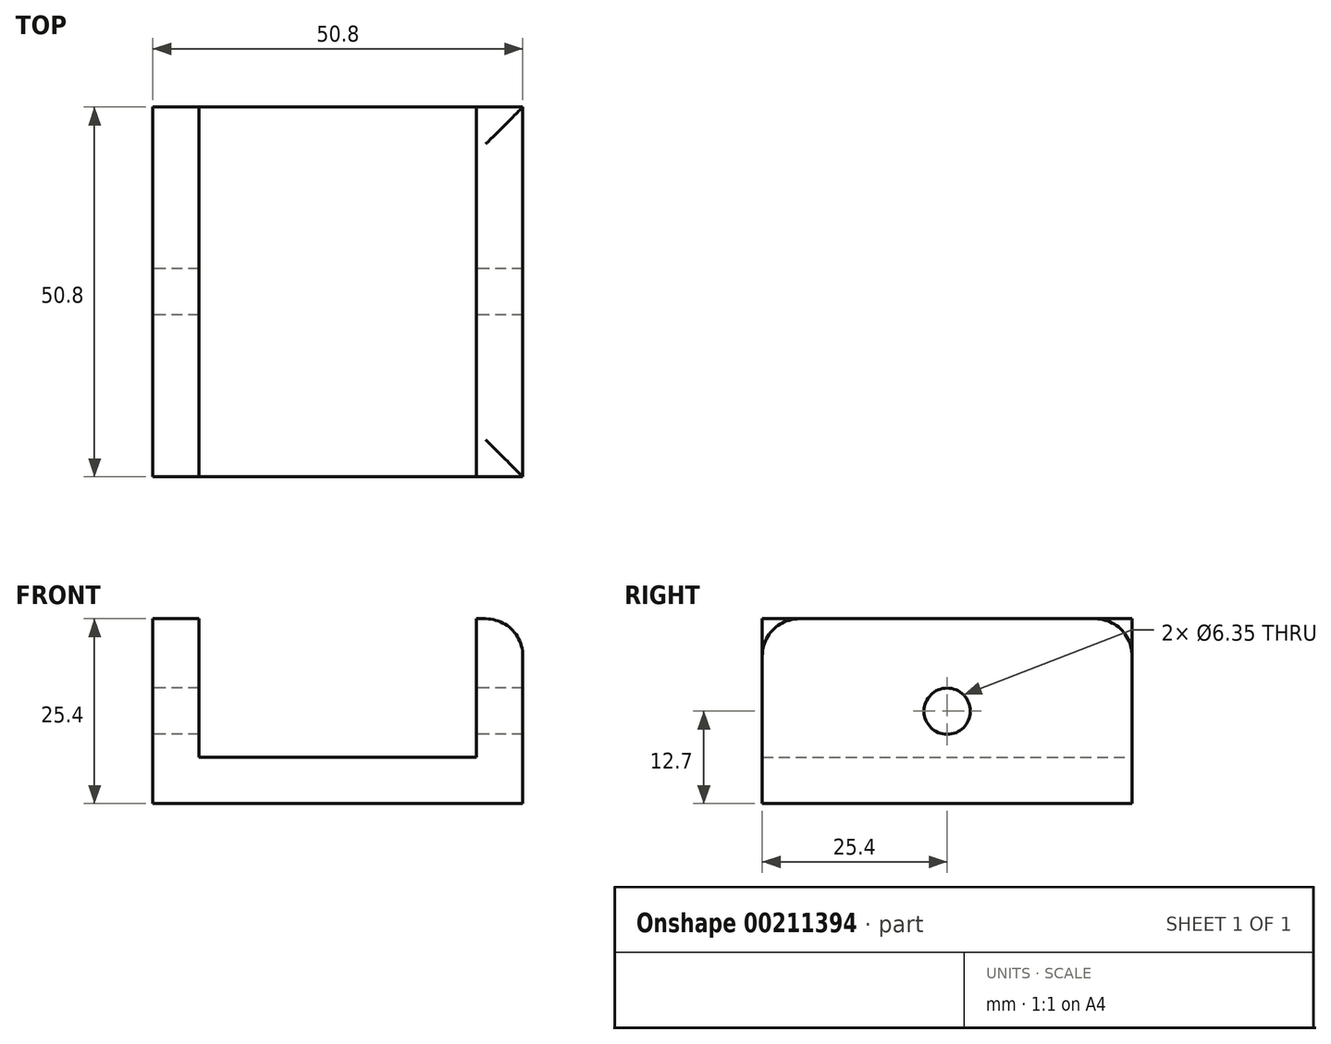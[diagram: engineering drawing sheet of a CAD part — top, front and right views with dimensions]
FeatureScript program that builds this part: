
annotation { "Feature Type Name" : "Feature", "Feature Type Description" : "" }
export const myFeature = defineFeature(function(context is Context, id is Id, definition is map)
    precondition{}
    {
        {
            var Q0;
            Q0=qCreatedBy(makeId("Front.planeOp"),FACE);
            var sketch = newSketch(context, id + "F0", { "sketchPlane" : qUnion([Q0])});
            skLineSegment(sketch, "E0", {"start": v(6.35, 25.4) * mm, "end": v(0, 25.4) * mm});
            skLineSegment(sketch, "E1", {"start": v(0, 25.4) * mm, "end": v(0, 0) * mm});
            skLineSegment(sketch, "E2", {"start": v(0, 0) * mm, "end": v(50.8, 0) * mm});
            skLineSegment(sketch, "E3", {"start": v(50.8, 0) * mm, "end": v(50.8, 25.4) * mm});
            skLineSegment(sketch, "E4", {"start": v(50.8, 25.4) * mm, "end": v(44.45, 25.4) * mm});
            skLineSegment(sketch, "E5", {"start": v(44.45, 25.4) * mm, "end": v(44.45, 6.35) * mm});
            skLineSegment(sketch, "E6", {"start": v(44.45, 6.35) * mm, "end": v(6.35, 6.35) * mm});
            skLineSegment(sketch, "E7", {"start": v(6.35, 6.35) * mm, "end": v(6.35, 25.4) * mm});
            skSolve(sketch);
        }
        {
            var Q0;
            Q0 = qSketchRegion(id + "F0", true);
            extrude(context, id + "F1", {"entities" : qUnion([Q0]), "depth" : 50.8 * mm});
        }
        {
            var Q0;
            Q0=makeQuery(id+"F1.opExtrude","SWEPT_FACE",FACE,{"disambiguationData":[OSD([sQuery(id+"F0.wireOp",EDGE,"E1")])]});
            var sketch = newSketch(context, id + "F2", { "sketchPlane" : qUnion([Q0])});
            skCircle(sketch, "E8", {"center": v(25.4, 12.7) * mm, "radius": 3.18 * mm});
            skPoint(sketch, "E8.centerSnap0", {"position": v(50.8, 12.7) * mm});
            skPoint(sketch, "E8.centerSnap1", {"position": v(25.4, 25.4) * mm});
            skSolve(sketch);
        }
        {
            var Q0;
            Q0=sQuery(id+"F2.wireOp",VERTEX,"E8.center");
            var Q1;
            Q1=makeQuery(id+"F1.opExtrude","SWEPT_BODY",BODY,{"disambiguationData":[OSD([sQuery(id+"F0.wireOp",EDGE,"E0"),sQuery(id+"F0.wireOp",EDGE,"E1"),sQuery(id+"F0.wireOp",EDGE,"E2"),sQuery(id+"F0.wireOp",EDGE,"E3"),sQuery(id+"F0.wireOp",EDGE,"E4"),sQuery(id+"F0.wireOp",EDGE,"E5"),sQuery(id+"F0.wireOp",EDGE,"E6"),sQuery(id+"F0.wireOp",EDGE,"E7")])]});
            hole(context, id + "F3", {"style" : HoleStyle.SIMPLE, "endStyle" : HoleEndStyle.THROUGH, "holeDiameter" : 6.35 * mm, "locations" : qUnion([Q0]), "scope" : qUnion([Q1]), "isTappedThrough" : true});
        }
        {
            var Q0;
            Q0=makeQuery(id+"F1.opExtrude","SWEPT_EDGE",EDGE,{"disambiguationData":[OSD([sQuery(id+"F0.wireOp",EDGE,"E3"),sQuery(id+"F0.wireOp",EDGE,"E4")])]});
            var Q1;
            Q1=makeQuery(id+"F1.opExtrude","CAP_EDGE",EDGE,{"disambiguationData":[OSD([sQuery(id+"F0.wireOp",EDGE,"E4")])],"isStart":false});
            var Q2;
            Q2=makeQuery(id+"F1.opExtrude","CAP_EDGE",EDGE,{"disambiguationData":[OSD([sQuery(id+"F0.wireOp",EDGE,"E4")])],"isStart":true});
            fillet(context, id + "F4", {"entities" : qUnion([Q0, Q1, Q2]), "radius" : 5.08 * mm, "tangentPropagation" : true, "allowEdgeOverflow" : false});
        }
    });
